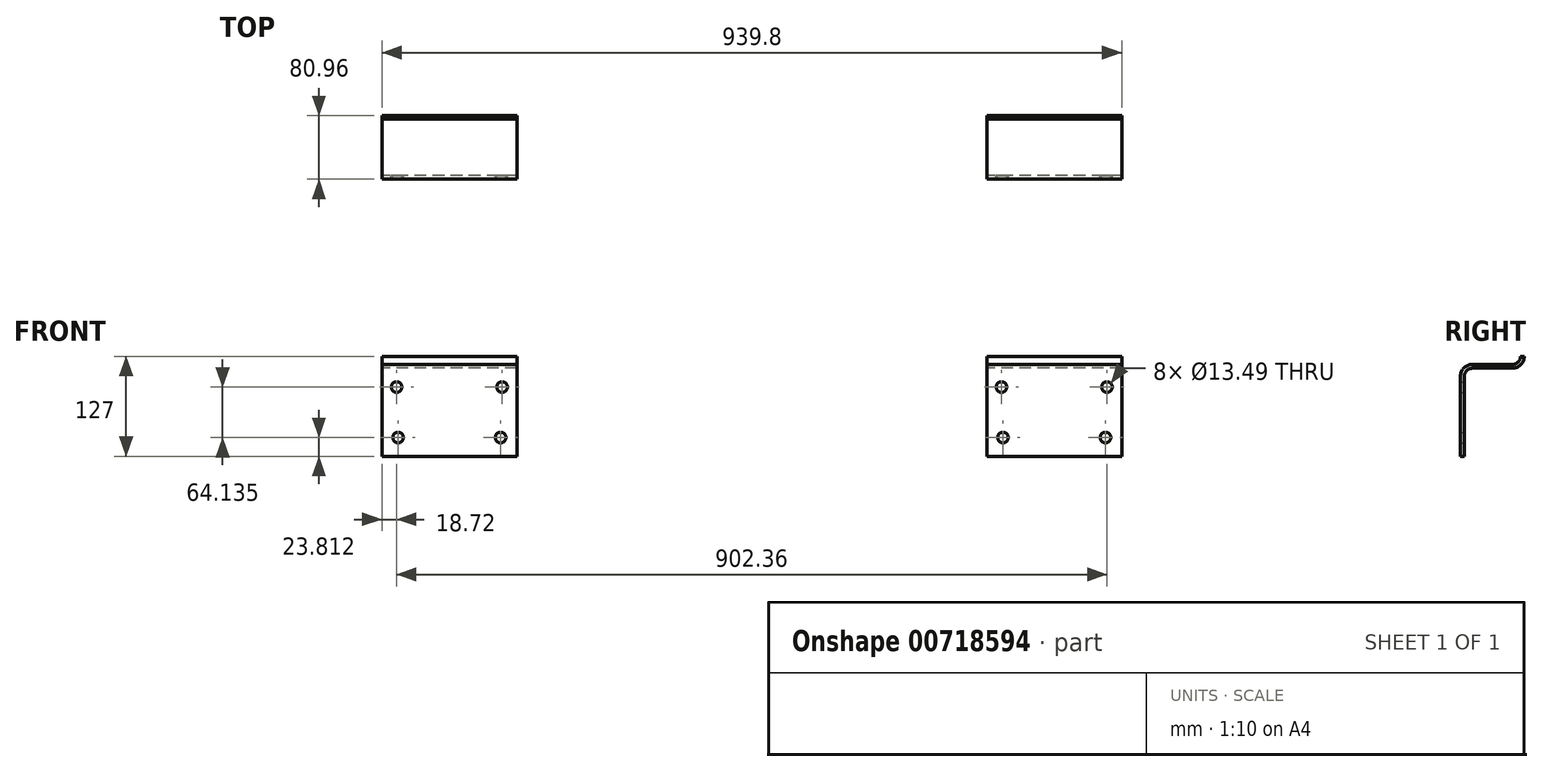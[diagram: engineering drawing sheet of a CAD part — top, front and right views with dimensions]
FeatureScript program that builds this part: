
annotation { "Feature Type Name" : "Feature", "Feature Type Description" : "" }
export const myFeature = defineFeature(function(context is Context, id is Id, definition is map)
    precondition{}
    {
        {
            var Q0;
            Q0=qCreatedBy(makeId("Right.planeOp"),FACE);
            var sketch = newSketch(context, id + "F0", { "sketchPlane" : qUnion([Q0])});
            skArc(sketch, "E0.MirrorCS", {"start": v(0, 101.6) * mm, "mid": v(3.72, 110.58) * mm, "end": v(12.7, 114.3) * mm});
            skArc(sketch, "E1.MirrorCS", {"start": v(63.5, 114.3) * mm, "mid": v(72.48, 118.02) * mm, "end": v(76.2, 127) * mm});
            skLineSegment(sketch, "E2.MirrorCS", {"start": v(12.7, 114.3) * mm, "end": v(63.5, 114.3) * mm});
            skLineSegment(sketch, "E3.MirrorCS", {"start": v(0, 0) * mm, "end": v(0, 101.6) * mm});
            skSolve(sketch);
        }
        {
            var Q0;
            Q0=qCreatedBy(makeId("Top.planeOp"),FACE);
            var sketch = newSketch(context, id + "F1", { "sketchPlane" : qUnion([Q0])});
            skLineSegment(sketch, "E4.bottom", {"start": v(85.73, 2.38) * mm, "end": v(-85.73, 2.38) * mm});
            skLineSegment(sketch, "E4.top", {"start": v(85.72, -2.38) * mm, "end": v(-85.72, -2.38) * mm});
            skLineSegment(sketch, "E4.left", {"start": v(85.73, 2.38) * mm, "end": v(85.73, -2.38) * mm});
            skLineSegment(sketch, "E4.right", {"start": v(-85.73, 2.38) * mm, "end": v(-85.73, -2.38) * mm});
            skPoint(sketch, "E4.middle", {"position": v(0, 0) * mm});
            skSolve(sketch);
        }
        {
            var Q0;
            Q0 = qSketchRegion(id + "F1", true);
            var Q1;
            Q1 = qSketchRegion(id + "F0", true);
            var Q2;
            Q2 = qConstructionFilter(qBodyType(qCreatedBy(id + "F0" ,EDGE), BodyType.WIRE), ConstructionObject.NO);
            sweep(context, id + "F2", {"profiles" : qUnion([Q0, Q1]), "path" : qUnion([Q2])});
        }
        {
            var Q0;
            Q0=makeQuery(id+"F2.opSweep","SWEPT_FACE",FACE,{"disambiguationData":[OSD([sQuery(id+"F0.wireOp",EDGE,"E3.MirrorCS"),sQuery(id+"F1.wireOp",EDGE,"E4.top")])]});
            var sketch = newSketch(context, id + "F3", { "sketchPlane" : qUnion([Q0])});
            skLineSegment(sketch, "E5", {"start": v(0, 101.6) * mm, "end": v(0, 0) * mm, "construction": true});
            skLineSegment(sketch, "E6", {"start": v(-67, 87.95) * mm, "end": v(0, 87.95) * mm, "construction": true});
            skLineSegment(sketch, "E7", {"start": v(67, 87.95) * mm, "end": v(0, 87.95) * mm, "construction": true});
            skLineSegment(sketch, "E8", {"start": v(-65.14, 23.81) * mm, "end": v(0, 23.81) * mm, "construction": true});
            skLineSegment(sketch, "E9", {"start": v(0, 23.81) * mm, "end": v(65.14, 23.81) * mm, "construction": true});
            skSolve(sketch);
        }
        {
            var Q0;
            Q0=makeQuery(id+"F2.opSweep","SWEPT_BODY",BODY,{"disambiguationData":[OSD([sQuery(id+"F0.wireOp",EDGE,"E3.MirrorCS"),sQuery(id+"F1.wireOp",EDGE,"E4.bottom"),sQuery(id+"F1.wireOp",EDGE,"E4.top"),sQuery(id+"F1.wireOp",EDGE,"E4.left"),sQuery(id+"F1.wireOp",EDGE,"E4.right")])]});
            transform(context, id + "F4", {"entities" : qUnion([Q0]), "transformType" : TransformType.TRANSLATION_3D, "dx" : 768.35 * mm, "dy" : 0 * mm, "dz" : 0 * mm, "makeCopy" : true});
        }
        {
            var Q0;
            Q0=makeQuery(id+"F4.opPattern","COPY",BODY,{"derivedFrom":makeQuery(id+"F2.opSweep","SWEPT_BODY",BODY,{"disambiguationData":[OSD([sQuery(id+"F0.wireOp",EDGE,"E3.MirrorCS"),sQuery(id+"F1.wireOp",EDGE,"E4.bottom"),sQuery(id+"F1.wireOp",EDGE,"E4.top"),sQuery(id+"F1.wireOp",EDGE,"E4.left"),sQuery(id+"F1.wireOp",EDGE,"E4.right")])]}),"instanceName":"1"});
            deleteBodies(context, id + "F5", {"entities" : qUnion([Q0])});
        }
        {
            var Q0;
            Q0=sQuery(id+"F3.wireOp",VERTEX,"E6.start");
            var Q1;
            Q1=sQuery(id+"F3.wireOp",VERTEX,"E7.start");
            var Q2;
            Q2=sQuery(id+"F3.wireOp",VERTEX,"E9.end");
            var Q3;
            Q3=sQuery(id+"F3.wireOp",VERTEX,"E8.start");
            var Q4;
            Q4=makeQuery(id+"F2.opSweep","SWEPT_BODY",BODY,{"disambiguationData":[OSD([sQuery(id+"F0.wireOp",EDGE,"E3.MirrorCS"),sQuery(id+"F1.wireOp",EDGE,"E4.bottom"),sQuery(id+"F1.wireOp",EDGE,"E4.top"),sQuery(id+"F1.wireOp",EDGE,"E4.left"),sQuery(id+"F1.wireOp",EDGE,"E4.right")])]});
            hole(context, id + "F6", {"style" : HoleStyle.SIMPLE, "endStyle" : HoleEndStyle.THROUGH, "standardTappedOrClearance" : lookupTablePath({ "standard" : "ANSI", "fit" : "Normal (ASME)", "size" : "1/2", "type" : "Clearance" }), "standardBlindInLast" : lookupTablePath({ "fit" : "Free", "standard" : "ANSI", "size" : "1/2", "type" : "Clearance" }), "holeDiameter" : 13.5 * mm, "majorDiameter" : 6.35 * mm, "isTappedThrough" : true, "tappedDepth" : 12.7 * mm, "tapClearance" : 3, "locations" : qUnion([Q0, Q1, Q2, Q3]), "scope" : qUnion([Q4]), "startStyle" : HoleStartStyle.PART});
        }
        {
            var Q0;
            Q0=makeQuery(id+"F2.opSweep","SWEPT_BODY",BODY,{"disambiguationData":[OSD([sQuery(id+"F0.wireOp",EDGE,"E3.MirrorCS"),sQuery(id+"F1.wireOp",EDGE,"E4.bottom"),sQuery(id+"F1.wireOp",EDGE,"E4.top"),sQuery(id+"F1.wireOp",EDGE,"E4.left"),sQuery(id+"F1.wireOp",EDGE,"E4.right")])]});
            var Q1;
            Q1=makeQuery(id+"F2.opSweep","CAP_EDGE",EDGE,{"disambiguationData":[OSD([sQuery(id+"F0.wireOp",VERTEX,"E3.MirrorCS.start"),sQuery(id+"F1.wireOp",EDGE,"E4.top")])],"isStart":true});
            var Q2;
            Q2=sQuery(id+"F3.wireOp",VERTEX,"E6.start");
            var Q3;
            Q3=makeQuery(id+"F2.opSweep","CAP_EDGE",EDGE,{"disambiguationData":[OSD([sQuery(id+"F0.wireOp",VERTEX,"E3.MirrorCS.start"),sQuery(id+"F1.wireOp",EDGE,"E4.top")])],"isStart":true});
            transform(context, id + "F7", {"entities" : qUnion([Q0]), "transformType" : TransformType.TRANSLATION_DISTANCE, "transformDirection" : qUnion([Q3]), "distance" : 384.17 * mm, "oppositeDirection" : true, "makeCopy" : true});
        }
        {
            var Q0;
            Q0=makeQuery(id+"F2.opSweep","SWEPT_BODY",BODY,{"disambiguationData":[OSD([sQuery(id+"F0.wireOp",EDGE,"E3.MirrorCS"),sQuery(id+"F1.wireOp",EDGE,"E4.bottom"),sQuery(id+"F1.wireOp",EDGE,"E4.top"),sQuery(id+"F1.wireOp",EDGE,"E4.left"),sQuery(id+"F1.wireOp",EDGE,"E4.right")])]});
            var Q1;
            Q1=makeQuery(id+"F2.opSweep","CAP_EDGE",EDGE,{"disambiguationData":[OSD([sQuery(id+"F0.wireOp",VERTEX,"E3.MirrorCS.start"),sQuery(id+"F1.wireOp",EDGE,"E4.top")])],"isStart":true});
            transform(context, id + "F8", {"entities" : qUnion([Q0]), "transformType" : TransformType.TRANSLATION_DISTANCE, "transformDirection" : qUnion([Q1]), "distance" : 384.17 * mm, "makeCopy" : false});
        }
    });
